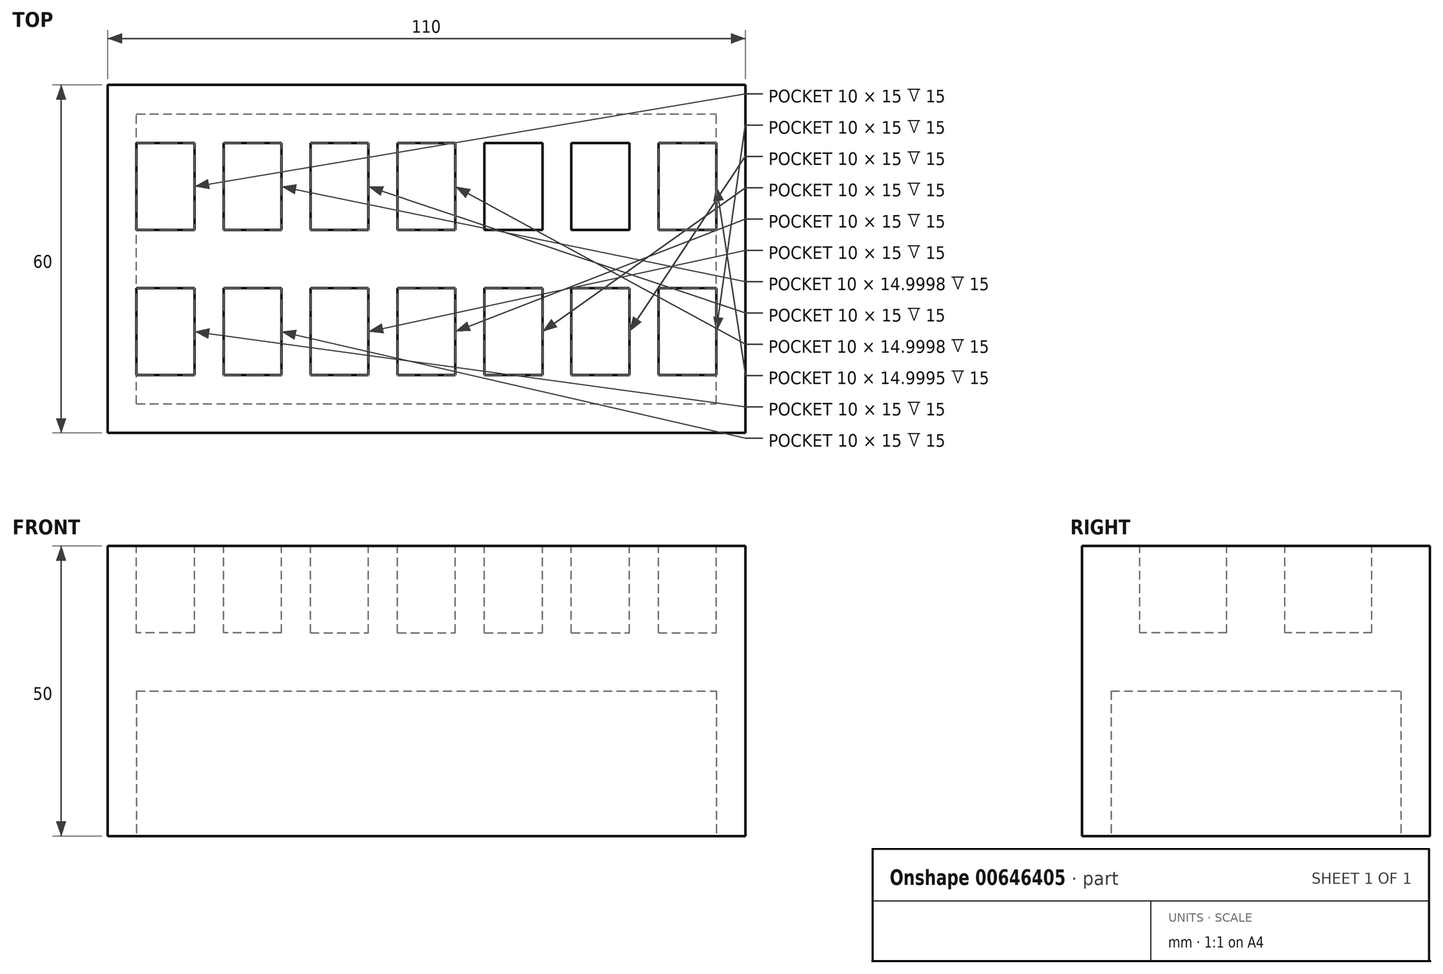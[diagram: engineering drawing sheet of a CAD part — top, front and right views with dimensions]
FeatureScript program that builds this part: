
annotation { "Feature Type Name" : "Feature", "Feature Type Description" : "" }
export const myFeature = defineFeature(function(context is Context, id is Id, definition is map)
    precondition{}
    {
        {
            var Q0;
            Q0=qCreatedBy(makeId("Top.planeOp"),FACE);
            var sketch = newSketch(context, id + "F0", { "sketchPlane" : qUnion([Q0])});
            skLineSegment(sketch, "E0.bottom", {"start": v(-53.55, 41.06) * mm, "end": v(56.45, 41.06) * mm});
            skLineSegment(sketch, "E0.top", {"start": v(-53.55, -18.94) * mm, "end": v(56.45, -18.94) * mm});
            skLineSegment(sketch, "E0.left", {"start": v(-53.55, 41.06) * mm, "end": v(-53.55, -18.94) * mm});
            skLineSegment(sketch, "E0.right", {"start": v(56.45, 41.06) * mm, "end": v(56.45, -18.94) * mm});
            skSolve(sketch);
        }
        {
            var Q0;
            Q0=makeQuery(id+"F0.imprint","IMPRINT",FACE,{"disambiguationData":[TD([[makeQuery(id+"F0.imprint","IMPRINT",EDGE,{"derivedFrom":sQuery(id+"F0.wireOp",EDGE,"E0.bottom")}),-1.0]])]});
            extrude(context, id + "F1", {"entities" : qUnion([Q0]), "depth" : 50 * mm, "offsetDistance" : 25 * mm});
        }
        {
            var Q0;
            Q0=makeQuery(id+"F1.opExtrude","CAP_FACE",FACE,{"disambiguationData":[OSD([sQuery(id+"F0.wireOp",EDGE,"E0.bottom"),sQuery(id+"F0.wireOp",EDGE,"E0.top"),sQuery(id+"F0.wireOp",EDGE,"E0.left"),sQuery(id+"F0.wireOp",EDGE,"E0.right")])],"isStart":true});
            var sketch = newSketch(context, id + "F2", { "sketchPlane" : qUnion([Q0])});
            skLineSegment(sketch, "E1", {"start": v(-53.55, 18.94) * mm, "end": v(-53.55, 13.94) * mm});
            skLineSegment(sketch, "E2", {"start": v(-53.55, -41.06) * mm, "end": v(-53.55, -36.06) * mm});
            skLineSegment(sketch, "E3", {"start": v(-53.55, 13.94) * mm, "end": v(-48.55, 13.94) * mm});
            skLineSegment(sketch, "E4", {"start": v(-53.55, -36.06) * mm, "end": v(-48.55, -36.06) * mm});
            skLineSegment(sketch, "E5.bottom", {"start": v(-48.55, 13.94) * mm, "end": v(51.45, 13.94) * mm});
            skLineSegment(sketch, "E5.top", {"start": v(-48.55, -36.06) * mm, "end": v(51.45, -36.06) * mm});
            skLineSegment(sketch, "E5.left", {"start": v(-48.55, 13.94) * mm, "end": v(-48.55, -36.06) * mm});
            skLineSegment(sketch, "E5.right", {"start": v(51.45, 13.94) * mm, "end": v(51.45, -36.06) * mm});
            skSolve(sketch);
        }
        {
            var Q0;
            Q0=makeQuery(id+"F2.imprint","IMPRINT",FACE,{"disambiguationData":[TD([[makeQuery(id+"F2.imprint","IMPRINT",EDGE,{"derivedFrom":sQuery(id+"F2.wireOp",EDGE,"E5.bottom")}),-1.0]])]});
            extrude(context, id + "F3", {"entities" : qUnion([Q0]), "operationType" : NewBodyOperationType.REMOVE, "oppositeDirection" : true, "depth" : 25 * mm, "offsetDistance" : 25 * mm});
        }
        {
            var Q0;
            Q0=makeQuery(id+"F1.opExtrude","CAP_FACE",FACE,{"disambiguationData":[OSD([sQuery(id+"F0.wireOp",EDGE,"E0.bottom"),sQuery(id+"F0.wireOp",EDGE,"E0.top"),sQuery(id+"F0.wireOp",EDGE,"E0.left"),sQuery(id+"F0.wireOp",EDGE,"E0.right")])],"isStart":false});
            var sketch = newSketch(context, id + "F4", { "sketchPlane" : qUnion([Q0])});
            skLineSegment(sketch, "E6", {"start": v(-38.55, -8.94) * mm, "end": v(-38.55, 6.06) * mm});
            skLineSegment(sketch, "E7", {"start": v(-38.55, 16.06) * mm, "end": v(-38.55, 31.06) * mm});
            skLineSegment(sketch, "E8", {"start": v(-23.55, 16.06) * mm, "end": v(-23.55, 31.06) * mm});
            skLineSegment(sketch, "E9", {"start": v(-23.55, 6.06) * mm, "end": v(-23.55, -8.94) * mm});
            skLineSegment(sketch, "E10", {"start": v(-8.55, 16.06) * mm, "end": v(-8.55, 31.06) * mm});
            skLineSegment(sketch, "E11", {"start": v(-8.55, 6.06) * mm, "end": v(-8.55, -8.94) * mm});
            skLineSegment(sketch, "E12", {"start": v(6.45, 16.06) * mm, "end": v(6.45, 31.06) * mm});
            skLineSegment(sketch, "E13", {"start": v(6.45, 6.06) * mm, "end": v(6.45, -8.94) * mm});
            skLineSegment(sketch, "E14", {"start": v(21.45, 16.06) * mm, "end": v(21.45, 31.06) * mm});
            skLineSegment(sketch, "E15", {"start": v(21.45, 6.06) * mm, "end": v(21.45, -8.94) * mm});
            skLineSegment(sketch, "E16", {"start": v(36.45, 16.06) * mm, "end": v(36.45, 31.06) * mm});
            skLineSegment(sketch, "E17", {"start": v(36.45, 6.06) * mm, "end": v(36.45, -8.94) * mm});
            skLineSegment(sketch, "E18", {"start": v(51.45, 16.06) * mm, "end": v(51.45, 31.06) * mm});
            skLineSegment(sketch, "E19", {"start": v(51.45, 6.06) * mm, "end": v(51.45, -8.94) * mm});
            skLineSegment(sketch, "E20.left", {"start": v(-38.55, 31.06) * mm, "end": v(-38.55, 16.06) * mm});
            skLineSegment(sketch, "E21.left", {"start": v(-38.55, 6.06) * mm, "end": v(-38.55, -8.94) * mm});
            skSolve(sketch);
        }
        {
            var Q0;
            Q0=makeQuery(id+"F4.imprint","IMPRINT",FACE,{"disambiguationData":[TD([[makeQuery(id+"F4.imprint","IMPRINT",EDGE,{"derivedFrom":makeQuery(id+"F1.opExtrude","CAP_EDGE",EDGE,{"disambiguationData":[OSD([sQuery(id+"F0.wireOp",EDGE,"E0.bottom")])],"isStart":false})}),-1.0]])]});
            var sketch = newSketch(context, id + "F5", { "sketchPlane" : qUnion([Q0])});
            skPoint(sketch, "E22", {"position": v(-38.55, 31.06) * mm});
            skPoint(sketch, "E23", {"position": v(-23.55, 31.06) * mm});
            skPoint(sketch, "E24", {"position": v(-8.55, 31.06) * mm});
            skPoint(sketch, "E25", {"position": v(6.45, 31.06) * mm});
            skPoint(sketch, "E26", {"position": v(21.45, 31.06) * mm});
            skPoint(sketch, "E27", {"position": v(36.45, 31.06) * mm});
            skPoint(sketch, "E28", {"position": v(51.45, 31.06) * mm});
            skLineSegment(sketch, "E29.bottom", {"start": v(-38.55, 31.06) * mm, "end": v(-48.55, 31.06) * mm});
            skLineSegment(sketch, "E29.top", {"start": v(-38.55, 16.06) * mm, "end": v(-48.55, 16.06) * mm});
            skLineSegment(sketch, "E29.left", {"start": v(-38.55, 31.06) * mm, "end": v(-38.55, 16.06) * mm});
            skLineSegment(sketch, "E29.right", {"start": v(-48.55, 31.06) * mm, "end": v(-48.55, 16.06) * mm});
            skLineSegment(sketch, "E30.bottom", {"start": v(-23.55, 31.06) * mm, "end": v(-33.55, 31.06) * mm});
            skLineSegment(sketch, "E30.top", {"start": v(-23.55, 16.06) * mm, "end": v(-33.55, 16.06) * mm});
            skLineSegment(sketch, "E30.left", {"start": v(-23.55, 31.06) * mm, "end": v(-23.55, 16.06) * mm});
            skLineSegment(sketch, "E30.right", {"start": v(-33.55, 31.06) * mm, "end": v(-33.55, 16.06) * mm});
            skLineSegment(sketch, "E31.bottom", {"start": v(-8.55, 31.06) * mm, "end": v(-18.55, 31.06) * mm});
            skLineSegment(sketch, "E31.top", {"start": v(-8.55, 16.06) * mm, "end": v(-18.55, 16.06) * mm});
            skLineSegment(sketch, "E31.left", {"start": v(-8.55, 31.06) * mm, "end": v(-8.55, 16.06) * mm});
            skLineSegment(sketch, "E31.right", {"start": v(-18.55, 31.06) * mm, "end": v(-18.55, 16.06) * mm});
            skLineSegment(sketch, "E32.bottom", {"start": v(6.45, 31.06) * mm, "end": v(-3.55, 31.06) * mm});
            skLineSegment(sketch, "E32.top", {"start": v(6.45, 16.06) * mm, "end": v(-3.55, 16.06) * mm});
            skLineSegment(sketch, "E32.left", {"start": v(6.45, 31.06) * mm, "end": v(6.45, 16.06) * mm});
            skLineSegment(sketch, "E32.right", {"start": v(-3.55, 31.06) * mm, "end": v(-3.55, 16.06) * mm});
            skLineSegment(sketch, "E33.bottom", {"start": v(21.45, 31.06) * mm, "end": v(11.45, 31.06) * mm});
            skLineSegment(sketch, "E33.top", {"start": v(21.45, 16.06) * mm, "end": v(11.45, 16.06) * mm});
            skLineSegment(sketch, "E33.left", {"start": v(21.45, 31.06) * mm, "end": v(21.45, 16.06) * mm});
            skLineSegment(sketch, "E33.right", {"start": v(11.45, 31.06) * mm, "end": v(11.45, 16.06) * mm});
            skLineSegment(sketch, "E34.bottom", {"start": v(36.45, 31.06) * mm, "end": v(26.45, 31.06) * mm});
            skLineSegment(sketch, "E34.top", {"start": v(36.45, 16.06) * mm, "end": v(26.45, 16.06) * mm});
            skLineSegment(sketch, "E34.left", {"start": v(36.45, 31.06) * mm, "end": v(36.45, 16.06) * mm});
            skLineSegment(sketch, "E34.right", {"start": v(26.45, 31.06) * mm, "end": v(26.45, 16.06) * mm});
            skLineSegment(sketch, "E35.bottom", {"start": v(51.45, 31.06) * mm, "end": v(41.45, 31.06) * mm});
            skLineSegment(sketch, "E35.top", {"start": v(51.45, 16.06) * mm, "end": v(41.45, 16.06) * mm});
            skLineSegment(sketch, "E35.left", {"start": v(51.45, 31.06) * mm, "end": v(51.45, 16.06) * mm});
            skLineSegment(sketch, "E35.right", {"start": v(41.45, 31.06) * mm, "end": v(41.45, 16.06) * mm});
            skLineSegment(sketch, "E36.bottom", {"start": v(-48.55, 6.06) * mm, "end": v(-38.55, 6.06) * mm});
            skLineSegment(sketch, "E36.top", {"start": v(-48.55, -8.94) * mm, "end": v(-38.55, -8.94) * mm});
            skLineSegment(sketch, "E36.left", {"start": v(-48.55, 6.06) * mm, "end": v(-48.55, -8.94) * mm});
            skLineSegment(sketch, "E36.right", {"start": v(-38.55, 6.06) * mm, "end": v(-38.55, -8.94) * mm});
            skLineSegment(sketch, "E37.bottom", {"start": v(-33.55, 6.06) * mm, "end": v(-23.55, 6.06) * mm});
            skLineSegment(sketch, "E37.top", {"start": v(-33.55, -8.94) * mm, "end": v(-23.55, -8.94) * mm});
            skLineSegment(sketch, "E37.left", {"start": v(-33.55, 6.06) * mm, "end": v(-33.55, -8.94) * mm});
            skLineSegment(sketch, "E37.right", {"start": v(-23.55, 6.06) * mm, "end": v(-23.55, -8.94) * mm});
            skLineSegment(sketch, "E38.bottom", {"start": v(-18.55, 6.06) * mm, "end": v(-8.55, 6.06) * mm});
            skLineSegment(sketch, "E38.top", {"start": v(-18.55, -8.94) * mm, "end": v(-8.55, -8.94) * mm});
            skLineSegment(sketch, "E38.left", {"start": v(-18.55, 6.06) * mm, "end": v(-18.55, -8.94) * mm});
            skLineSegment(sketch, "E38.right", {"start": v(-8.55, 6.06) * mm, "end": v(-8.55, -8.94) * mm});
            skLineSegment(sketch, "E39.bottom", {"start": v(-3.55, 6.06) * mm, "end": v(6.45, 6.06) * mm});
            skLineSegment(sketch, "E39.top", {"start": v(-3.55, -8.94) * mm, "end": v(6.45, -8.94) * mm});
            skLineSegment(sketch, "E39.left", {"start": v(-3.55, 6.06) * mm, "end": v(-3.55, -8.94) * mm});
            skLineSegment(sketch, "E39.right", {"start": v(6.45, 6.06) * mm, "end": v(6.45, -8.94) * mm});
            skLineSegment(sketch, "E40.bottom", {"start": v(11.45, 6.06) * mm, "end": v(21.45, 6.06) * mm});
            skLineSegment(sketch, "E40.top", {"start": v(11.45, -8.94) * mm, "end": v(21.45, -8.94) * mm});
            skLineSegment(sketch, "E40.left", {"start": v(11.45, 6.06) * mm, "end": v(11.45, -8.94) * mm});
            skLineSegment(sketch, "E40.right", {"start": v(21.45, 6.06) * mm, "end": v(21.45, -8.94) * mm});
            skLineSegment(sketch, "E41.bottom", {"start": v(26.45, 6.06) * mm, "end": v(36.45, 6.06) * mm});
            skLineSegment(sketch, "E41.top", {"start": v(26.45, -8.94) * mm, "end": v(36.45, -8.94) * mm});
            skLineSegment(sketch, "E41.left", {"start": v(26.45, 6.06) * mm, "end": v(26.45, -8.94) * mm});
            skLineSegment(sketch, "E41.right", {"start": v(36.45, 6.06) * mm, "end": v(36.45, -8.94) * mm});
            skLineSegment(sketch, "E42.bottom", {"start": v(41.45, 6.06) * mm, "end": v(51.45, 6.06) * mm});
            skLineSegment(sketch, "E42.top", {"start": v(41.45, -8.94) * mm, "end": v(51.45, -8.94) * mm});
            skLineSegment(sketch, "E42.left", {"start": v(41.45, 6.06) * mm, "end": v(41.45, -8.94) * mm});
            skLineSegment(sketch, "E42.right", {"start": v(51.45, 6.06) * mm, "end": v(51.45, -8.94) * mm});
            skSolve(sketch);
        }
        {
            var Q0;
            Q0 = qSketchRegion(id + "F5", true);
            extrude(context, id + "F6", {"entities" : qUnion([Q0]), "operationType" : NewBodyOperationType.REMOVE, "oppositeDirection" : true, "depth" : 15 * mm, "offsetDistance" : 25 * mm});
        }
    });
